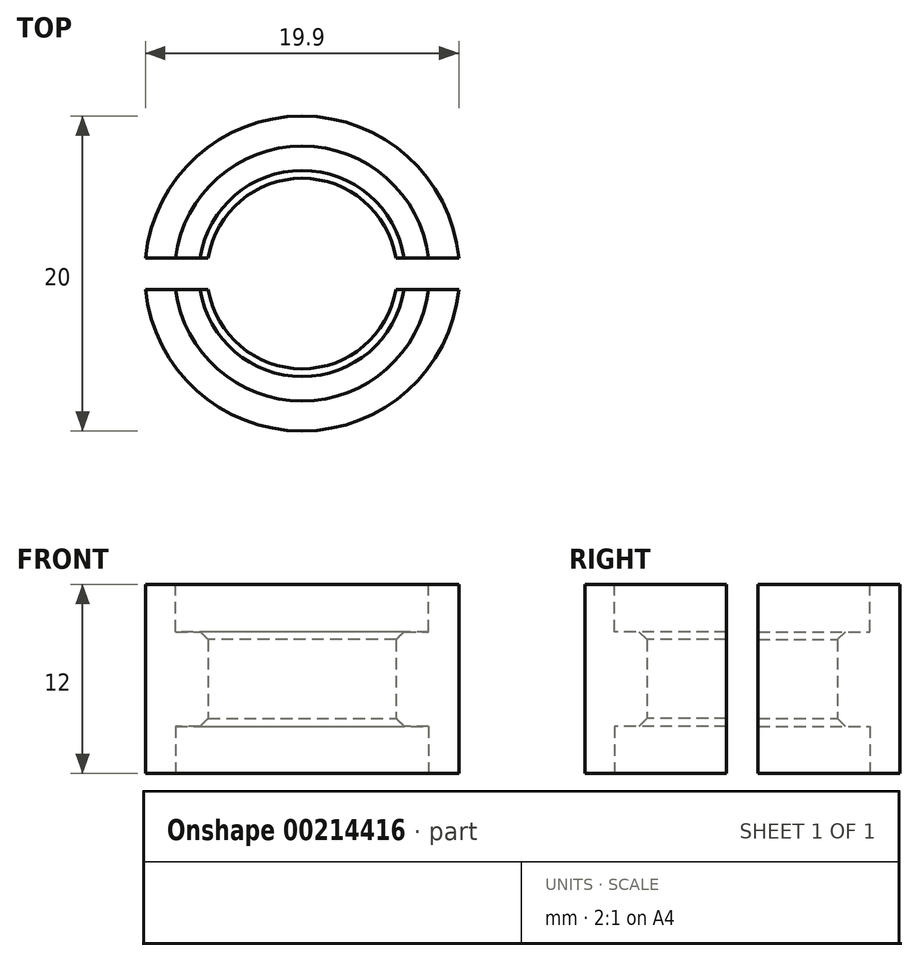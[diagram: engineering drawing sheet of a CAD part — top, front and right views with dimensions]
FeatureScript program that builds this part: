
annotation { "Feature Type Name" : "Feature", "Feature Type Description" : "" }
export const myFeature = defineFeature(function(context is Context, id is Id, definition is map)
    precondition{}
    {
        {
            var Q0;
            Q0=qCreatedBy(makeId("Top.planeOp"),FACE);
            var sketch = newSketch(context, id + "F0", { "sketchPlane" : qUnion([Q0])});
            skCircle(sketch, "E0", {"center": v(0, 0) * mm, "radius": 10 * mm});
            skCircle(sketch, "E1", {"center": v(0, 0) * mm, "radius": 6.05 * mm});
            skSolve(sketch);
        }
        {
            var Q0;
            Q0 = qSketchRegion(id + "F0", true);
            extrude(context, id + "F1", {"entities" : qUnion([Q0]), "depth" : 12 * mm});
        }
        {
            var Q0;
            Q0=makeQuery(id+"F1.opExtrude","CAP_FACE",FACE,{"disambiguationData":[OSD([sQuery(id+"F0.wireOp",EDGE,"E0"),sQuery(id+"F0.wireOp",EDGE,"E1")])],"isStart":false});
            var sketch = newSketch(context, id + "F2", { "sketchPlane" : qUnion([Q0])});
            skCircle(sketch, "E2", {"center": v(0, 0) * mm, "radius": 8.1 * mm});
            skSolve(sketch);
        }
        {
            var Q0;
            Q0 = qSketchRegion(id + "F2", true);
            extrude(context, id + "F3", {"entities" : qUnion([Q0]), "operationType" : NewBodyOperationType.REMOVE, "oppositeDirection" : true, "depth" : 3 * mm});
        }
        {
            var Q0;
            Q0=makeQuery(id+"F1.opExtrude","CAP_FACE",FACE,{"disambiguationData":[OSD([sQuery(id+"F0.wireOp",EDGE,"E0"),sQuery(id+"F0.wireOp",EDGE,"E1")])],"isStart":true});
            var sketch = newSketch(context, id + "F4", { "sketchPlane" : qUnion([Q0])});
            skCircle(sketch, "E3", {"center": v(0, 0) * mm, "radius": 8.1 * mm});
            skSolve(sketch);
        }
        {
            var Q0;
            Q0 = qSketchRegion(id + "F4", true);
            extrude(context, id + "F5", {"entities" : qUnion([Q0]), "operationType" : NewBodyOperationType.REMOVE, "oppositeDirection" : true, "depth" : 3 * mm});
        }
        {
            var Q0;
            Q0=makeQuery(id+"F5.boolean.opBoolean","INTERSECT",EDGE,{"derivedFrom":[makeQuery(id+"F1.opExtrude","SWEPT_FACE",FACE,{"disambiguationData":[OSD([sQuery(id+"F0.wireOp",EDGE,"E1")])]}),makeQuery(id+"F5.opExtrude","CAP_FACE",FACE,{"disambiguationData":[OSD([sQuery(id+"F4.wireOp",EDGE,"E3")])],"isStart":false})]});
            var Q1;
            Q1=makeQuery(id+"F3.boolean.opBoolean","INTERSECT",EDGE,{"derivedFrom":[makeQuery(id+"F1.opExtrude","SWEPT_FACE",FACE,{"disambiguationData":[OSD([sQuery(id+"F0.wireOp",EDGE,"E1")])]}),makeQuery(id+"F3.opExtrude","CAP_FACE",FACE,{"disambiguationData":[OSD([sQuery(id+"F2.wireOp",EDGE,"E2")])],"isStart":false})]});
            chamfer(context, id + "F6", {"entities" : qUnion([Q0, Q1]), "width" : 0.5 * mm, "tangentPropagation" : true});
        }
        {
            var Q0;
            Q0=makeQuery(id+"F1.opExtrude","CAP_FACE",FACE,{"disambiguationData":[OSD([sQuery(id+"F0.wireOp",EDGE,"E0"),sQuery(id+"F0.wireOp",EDGE,"E1")])],"isStart":false});
            var sketch = newSketch(context, id + "F7", { "sketchPlane" : qUnion([Q0])});
            skLineSegment(sketch, "E4.bottom", {"start": v(-12, 1) * mm, "end": v(12, 1) * mm});
            skLineSegment(sketch, "E4.top", {"start": v(-12, -1) * mm, "end": v(12, -1) * mm});
            skLineSegment(sketch, "E4.left", {"start": v(-12, 1) * mm, "end": v(-12, -1) * mm});
            skLineSegment(sketch, "E4.right", {"start": v(12, 1) * mm, "end": v(12, -1) * mm});
            skSolve(sketch);
        }
        {
            var Q0;
            Q0 = qSketchRegion(id + "F7", true);
            extrude(context, id + "F8", {"entities" : qUnion([Q0]), "operationType" : NewBodyOperationType.REMOVE, "endBound" : BoundingType.THROUGH_ALL, "oppositeDirection" : true, "depth" : 25 * mm});
        }
    });
